# Revit family: Original 1227 Mini Table Lamp
name_source: partatom
category: Lighting Fixtures
revit_build: Autodesk Revit 2016 (Build: 20150220_1215(x64)
units: mm (PartAtom-declared; Revit-internal decimal feet)

## family parameters
Always vertical = Yes
Cut with Voids When Loaded = No
Light Source = No
OmniClass Number = 23.80.70.11.14
OmniClass Title = General Luminaries, Directional
Part Type = Normal
Room Calculation Point = No
Round Connector Dimension = Use Diameter
Shared = No
Work Plane-Based = No

## types (1)
- Original 1227 Mini Table Lamp
    Brand URL = www.anglepoise.com
    Edition Number = Original 1227
    Energy Efficiency Class = Compatible with lamps from A+ to E
    IP Rating = IP20
    Lamp = E14 Lamp UK/EU  E12 Lamp US/CANADA
    Manufacturer Country = China
    Manufacturer Name = Anglepoise
    Material = Steel & Stainless Steel - Painted / Plated
    Material Main = Steel
    Material Secondary = Stainless Steel
    Mounting = Table Lamp
    Product Family = Table Lamp
    Wattage Comments = 6W Max LED  15W Max CFL
    Weight = 1.90Kg

## geometry (parser evidence)
native form markers: Sweep x3
no freeform markers — native parametric forms only
